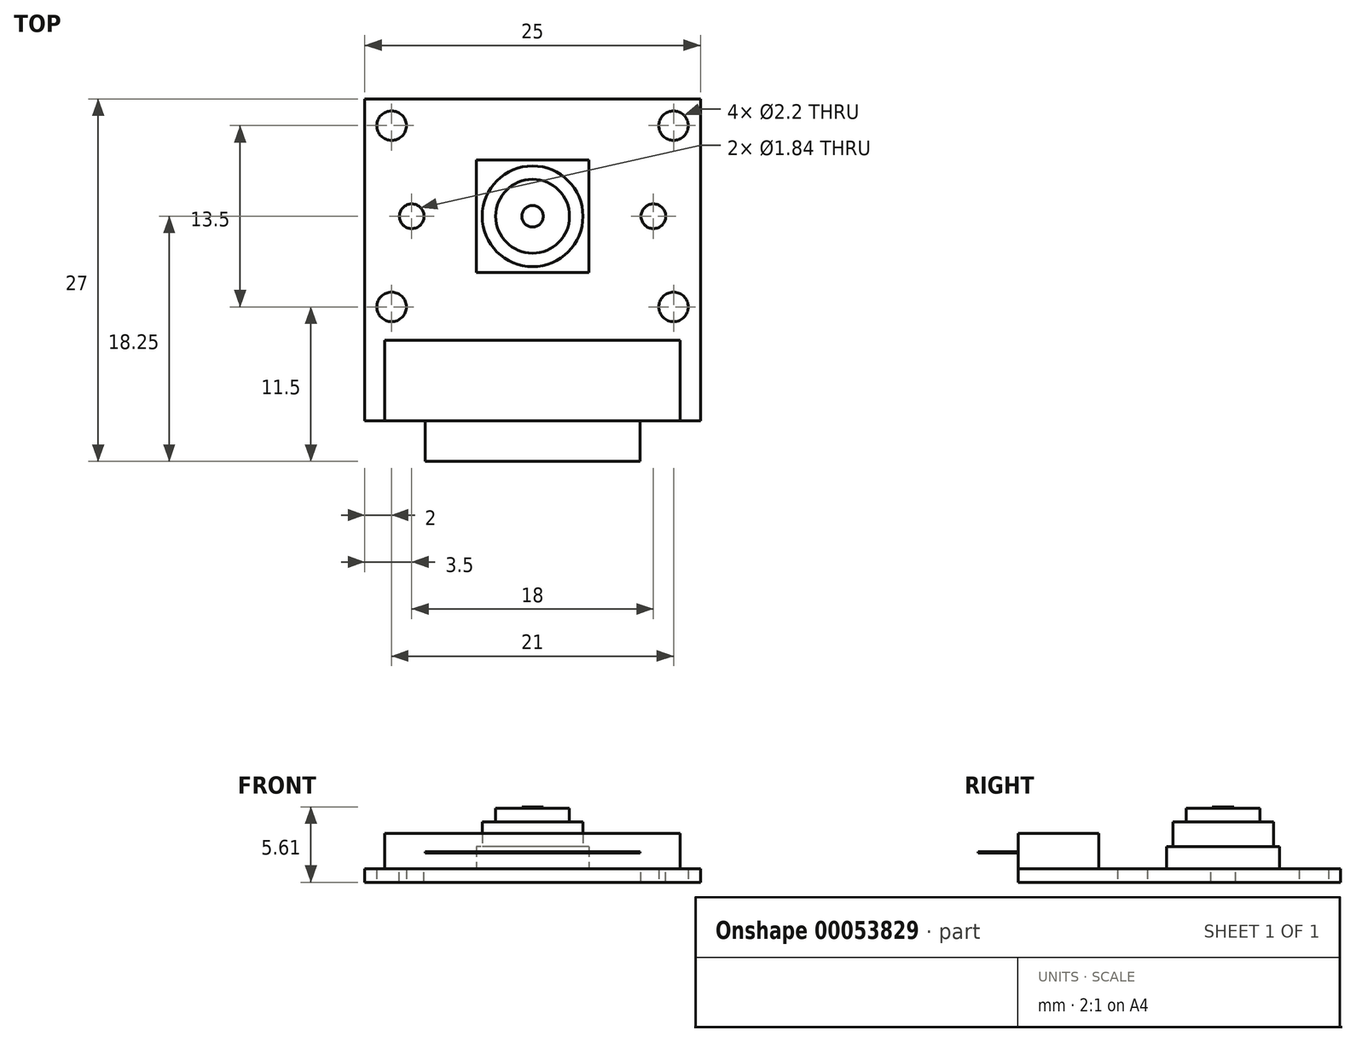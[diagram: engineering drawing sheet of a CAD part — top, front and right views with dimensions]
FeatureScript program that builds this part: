
annotation { "Feature Type Name" : "Feature", "Feature Type Description" : "" }
export const myFeature = defineFeature(function(context is Context, id is Id, definition is map)
    precondition{}
    {
        {
            var Q0;
            Q0=qCreatedBy(makeId("Top.planeOp"),FACE);
            var sketch = newSketch(context, id + "F0", { "sketchPlane" : qUnion([Q0])});
            skLineSegment(sketch, "E0.rect.bottom", {"start": v(12.5, 12) * mm, "end": v(-12.5, 12) * mm});
            skLineSegment(sketch, "E0.rect.top", {"start": v(12.5, -12) * mm, "end": v(-12.5, -12) * mm});
            skLineSegment(sketch, "E0.rect.left", {"start": v(12.5, 12) * mm, "end": v(12.5, -12) * mm});
            skLineSegment(sketch, "E0.rect.right", {"start": v(-12.5, 12) * mm, "end": v(-12.5, -12) * mm});
            skPoint(sketch, "E0.rect.middle", {"position": v(0, 0) * mm});
            skCircle(sketch, "E1", {"center": v(-10.5, 10) * mm, "radius": 1.1 * mm});
            skCircle(sketch, "E2", {"center": v(-10.5, -3.5) * mm, "radius": 1.1 * mm});
            skLineSegment(sketch, "E3", {"start": v(-10.5, 10) * mm, "end": v(-10.5, -12) * mm, "construction": true});
            skCircle(sketch, "E4.MirrorC", {"center": v(10.5, 10) * mm, "radius": 1.1 * mm});
            skCircle(sketch, "E5.MirrorC", {"center": v(10.5, -3.5) * mm, "radius": 1.1 * mm});
            skSolve(sketch);
        }
        {
            var Q0;
            Q0=makeQuery(id+"F0.imprint","IMPRINT",FACE,{"disambiguationData":[TD([[makeQuery(id+"F0.imprint","IMPRINT",EDGE,{"derivedFrom":sQuery(id+"F0.wireOp",EDGE,"E0.rect.bottom")}),1.0]])]});
            extrude(context, id + "F1", {"entities" : qUnion([Q0]), "depth" : 1 * mm});
        }
        {
            var Q0;
            Q0=makeQuery(id+"F1.opExtrude","CAP_FACE",FACE,{"disambiguationData":[OSD([sQuery(id+"F0.wireOp",EDGE,"E0.rect.bottom"),sQuery(id+"F0.wireOp",EDGE,"E0.rect.top"),sQuery(id+"F0.wireOp",EDGE,"E0.rect.left"),sQuery(id+"F0.wireOp",EDGE,"E0.rect.right"),sQuery(id+"F0.wireOp",EDGE,"E1"),sQuery(id+"F0.wireOp",EDGE,"E2"),sQuery(id+"F0.wireOp",EDGE,"E4.MirrorC"),sQuery(id+"F0.wireOp",EDGE,"E5.MirrorC")])],"isStart":false});
            var sketch = newSketch(context, id + "F2", { "sketchPlane" : qUnion([Q0])});
            skLineSegment(sketch, "E6", {"start": v(-12.5, 3.25) * mm, "end": v(12.5, 3.25) * mm, "construction": true});
            skLineSegment(sketch, "E7.rect.bottom", {"start": v(4.2, 7.45) * mm, "end": v(-4.2, 7.45) * mm});
            skLineSegment(sketch, "E7.rect.top", {"start": v(4.2, -0.95) * mm, "end": v(-4.2, -0.95) * mm});
            skLineSegment(sketch, "E7.rect.left", {"start": v(4.2, 7.45) * mm, "end": v(4.2, -0.95) * mm});
            skLineSegment(sketch, "E7.rect.right", {"start": v(-4.2, 7.45) * mm, "end": v(-4.2, -0.95) * mm});
            skPoint(sketch, "E7.rect.middle", {"position": v(0, 3.25) * mm});
            skCircle(sketch, "E8", {"center": v(0, 3.25) * mm, "radius": 3.75 * mm});
            skCircle(sketch, "E9", {"center": v(0, 3.25) * mm, "radius": 2.75 * mm});
            skLineSegment(sketch, "E10", {"start": v(-10.5, 10) * mm, "end": v(10.5, 10) * mm, "construction": true});
            skLineSegment(sketch, "E11", {"start": v(-10.5, -3.5) * mm, "end": v(10.5, -3.5) * mm, "construction": true});
            skCircle(sketch, "E12", {"center": v(-9, 3.25) * mm, "radius": 0.92 * mm});
            skCircle(sketch, "E13", {"center": v(9, 3.25) * mm, "radius": 0.92 * mm});
            skLineSegment(sketch, "E14", {"start": v(0, 10) * mm, "end": v(0, -3.5) * mm, "construction": true});
            skSolve(sketch);
        }
        {
            var Q0;
            Q0=makeQuery(id+"F2.imprint","IMPRINT",FACE,{"disambiguationData":[TD([[makeQuery(id+"F2.imprint","IMPRINT",EDGE,{"derivedFrom":sQuery(id+"F2.wireOp",EDGE,"E12")}),1.0]])]});
            var Q1;
            Q1=makeQuery(id+"F2.imprint","IMPRINT",FACE,{"disambiguationData":[TD([[makeQuery(id+"F2.imprint","IMPRINT",EDGE,{"derivedFrom":sQuery(id+"F2.wireOp",EDGE,"E13")}),1.0]])]});
            extrude(context, id + "F3", {"entities" : qUnion([Q0, Q1]), "operationType" : NewBodyOperationType.REMOVE, "endBound" : BoundingType.UP_TO_NEXT, "oppositeDirection" : true, "depth" : 25 * mm});
        }
        {
            var Q0;
            Q0=makeQuery(id+"F2.imprint","IMPRINT",FACE,{"disambiguationData":[TD([[makeQuery(id+"F2.imprint","IMPRINT",EDGE,{"derivedFrom":sQuery(id+"F2.wireOp",EDGE,"E7.rect.bottom")}),1.0]])]});
            var Q1;
            Q1=makeQuery(id+"F2.imprint","IMPRINT",FACE,{"disambiguationData":[TD([[makeQuery(id+"F2.imprint","IMPRINT",EDGE,{"derivedFrom":sQuery(id+"F2.wireOp",EDGE,"E8")}),1.0]])]});
            var Q2;
            Q2=makeQuery(id+"F2.imprint","IMPRINT",FACE,{"disambiguationData":[TD([[makeQuery(id+"F2.imprint","IMPRINT",EDGE,{"derivedFrom":sQuery(id+"F2.wireOp",EDGE,"E9")}),1.0]])]});
            extrude(context, id + "F4", {"entities" : qUnion([Q0, Q1, Q2]), "depth" : 1.65 * mm});
        }
        {
            var Q0;
            Q0=makeQuery(id+"F2.imprint","IMPRINT",FACE,{"disambiguationData":[TD([[makeQuery(id+"F2.imprint","IMPRINT",EDGE,{"derivedFrom":sQuery(id+"F2.wireOp",EDGE,"E8")}),1.0]])]});
            var Q1;
            Q1=makeQuery(id+"F2.imprint","IMPRINT",FACE,{"disambiguationData":[TD([[makeQuery(id+"F2.imprint","IMPRINT",EDGE,{"derivedFrom":sQuery(id+"F2.wireOp",EDGE,"E9")}),1.0]])]});
            extrude(context, id + "F5", {"entities" : qUnion([Q0, Q1]), "operationType" : NewBodyOperationType.ADD, "depth" : (1.65 + 1.86) * mm});
        }
        {
            var Q0;
            Q0=makeQuery(id+"F2.imprint","IMPRINT",FACE,{"disambiguationData":[TD([[makeQuery(id+"F2.imprint","IMPRINT",EDGE,{"derivedFrom":sQuery(id+"F2.wireOp",EDGE,"E9")}),1.0]])]});
            extrude(context, id + "F6", {"entities" : qUnion([Q0]), "operationType" : NewBodyOperationType.ADD, "depth" : (1.65 + 1.86 + 1) * mm});
        }
        {
            var Q0;
            Q0=makeQuery(id+"F6.opExtrude","CAP_FACE",FACE,{"disambiguationData":[OSD([sQuery(id+"F2.wireOp",EDGE,"E9")])],"isStart":false});
            var sketch = newSketch(context, id + "F7", { "sketchPlane" : qUnion([Q0])});
            skCircle(sketch, "E15", {"center": v(0, 3.25) * mm, "radius": 0.8 * mm});
            skSolve(sketch);
        }
        {
            var Q0;
            Q0=makeQuery(id+"F7.imprint","IMPRINT",FACE,{"disambiguationData":[TD([[makeQuery(id+"F7.imprint","IMPRINT",EDGE,{"derivedFrom":sQuery(id+"F7.wireOp",EDGE,"E15")}),1.0]])]});
            extrude(context, id + "F8", {"entities" : qUnion([Q0]), "depth" : 0.1 * mm});
        }
        {
            var Q0;
            Q0=makeQuery(id+"F2.imprint","IMPRINT",FACE,{"disambiguationData":[TD([[makeQuery(id+"F2.imprint","IMPRINT",EDGE,{"derivedFrom":sQuery(id+"F2.wireOp",EDGE,"E7.rect.bottom")}),-1.0]])]});
            var sketch = newSketch(context, id + "F9", { "sketchPlane" : qUnion([Q0])});
            skLineSegment(sketch, "E16.bottom", {"start": v(-11, -6) * mm, "end": v(11, -6) * mm});
            skLineSegment(sketch, "E16.top", {"start": v(-11, -12) * mm, "end": v(11, -12) * mm});
            skLineSegment(sketch, "E16.left", {"start": v(-11, -6) * mm, "end": v(-11, -12) * mm});
            skLineSegment(sketch, "E16.right", {"start": v(11, -6) * mm, "end": v(11, -12) * mm});
            skSolve(sketch);
        }
        {
            var Q0;
            Q0 = qSketchRegion(id + "F9", true);
            extrude(context, id + "F10", {"entities" : qUnion([Q0]), "depth" : 2.65 * mm});
        }
        {
            var Q0;
            Q0=makeQuery(id+"F1.opExtrude","CAP_FACE",FACE,{"disambiguationData":[OSD([sQuery(id+"F0.wireOp",EDGE,"E0.rect.bottom"),sQuery(id+"F0.wireOp",EDGE,"E0.rect.top"),sQuery(id+"F0.wireOp",EDGE,"E0.rect.left"),sQuery(id+"F0.wireOp",EDGE,"E0.rect.right"),sQuery(id+"F0.wireOp",EDGE,"E1"),sQuery(id+"F0.wireOp",EDGE,"E2"),sQuery(id+"F0.wireOp",EDGE,"E4.MirrorC"),sQuery(id+"F0.wireOp",EDGE,"E5.MirrorC")])],"isStart":true});
            cPlane(context, id + "F11", {"entities" : qUnion([Q0]), "cplaneType" : CPlaneType.OFFSET, "offset" : (2.65 / 2 + 0.95) * mm, "oppositeDirection" : true, "width" : 150 * mm, "height" : 150 * mm});
        }
        {
            var Q0;
            Q0=qCreatedBy(id+"F11.planeOp",FACE);
            var sketch = newSketch(context, id + "F12", { "sketchPlane" : qUnion([Q0])});
            skLineSegment(sketch, "E17.bottom", {"start": v(-8, 12) * mm, "end": v(8, 12) * mm});
            skLineSegment(sketch, "E17.top", {"start": v(-8, 15) * mm, "end": v(8, 15) * mm});
            skLineSegment(sketch, "E17.left", {"start": v(-8, 12) * mm, "end": v(-8, 15) * mm});
            skLineSegment(sketch, "E17.right", {"start": v(8, 12) * mm, "end": v(8, 15) * mm});
            skSolve(sketch);
        }
        {
            var Q0;
            Q0=makeQuery(id+"F12.imprint","IMPRINT",FACE,{"disambiguationData":[TD([[makeQuery(id+"F12.imprint","IMPRINT",EDGE,{"derivedFrom":sQuery(id+"F12.wireOp",EDGE,"E17.bottom")}),1.0]])]});
            extrude(context, id + "F13", {"entities" : qUnion([Q0]), "depth" : 0.1 * mm});
        }
    });
